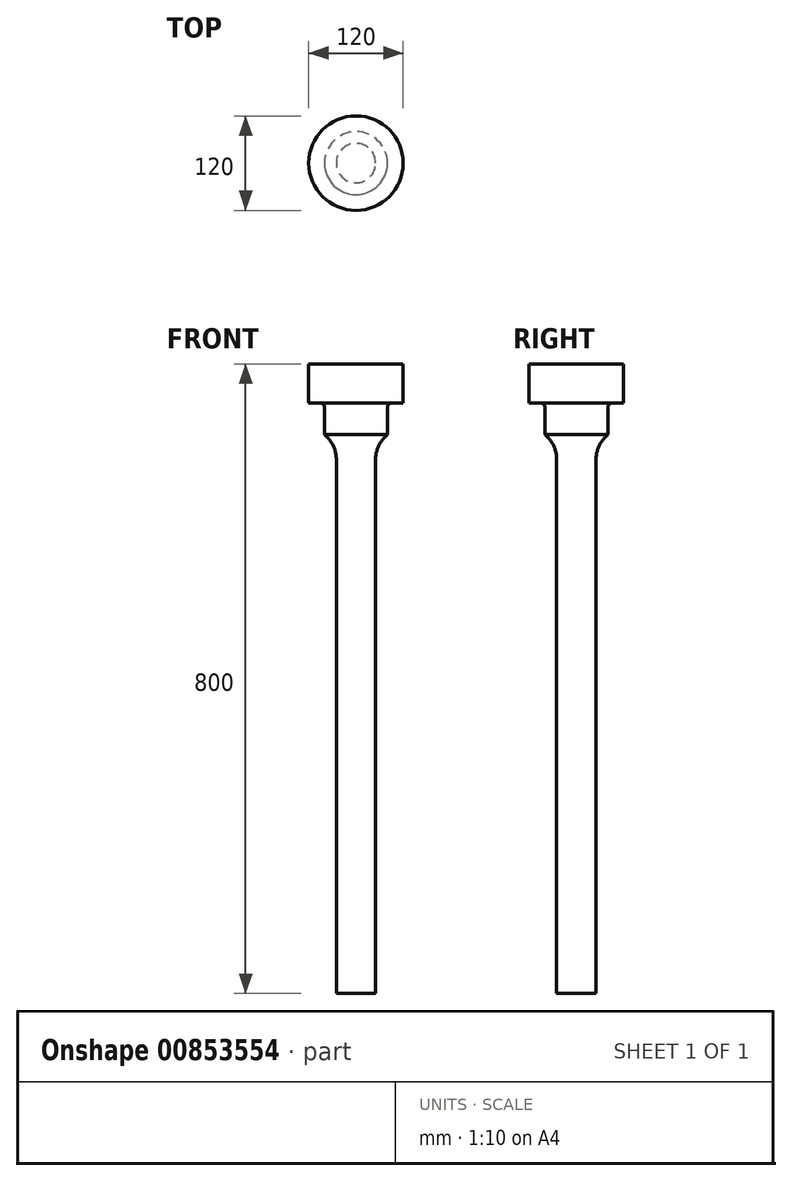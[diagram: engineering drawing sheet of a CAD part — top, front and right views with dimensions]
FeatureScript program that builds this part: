
annotation { "Feature Type Name" : "Feature", "Feature Type Description" : "" }
export const myFeature = defineFeature(function(context is Context, id is Id, definition is map)
    precondition{}
    {
        {
            var Q0;
            Q0=qCreatedBy(makeId("Front.planeOp"),FACE);
            var sketch = newSketch(context, id + "F0", { "sketchPlane" : qUnion([Q0])});
            skLineSegment(sketch, "E0", {"start": v(0, 0) * mm, "end": v(-60, 0) * mm});
            skLineSegment(sketch, "E1", {"start": v(-60, 0) * mm, "end": v(-60, -50) * mm});
            skLineSegment(sketch, "E2", {"start": v(-60, -50) * mm, "end": v(-40, -50) * mm});
            skLineSegment(sketch, "E3", {"start": v(-40, -50) * mm, "end": v(-40, -90) * mm});
            skLineSegment(sketch, "E4", {"start": v(-40, -90) * mm, "end": v(-25, -90) * mm});
            skLineSegment(sketch, "E5", {"start": v(-25, -90) * mm, "end": v(-25, -800) * mm});
            skLineSegment(sketch, "E6", {"start": v(-25, -800) * mm, "end": v(0, -800) * mm});
            skLineSegment(sketch, "E7", {"start": v(0, 0) * mm, "end": v(0, -800) * mm});
            skSolve(sketch);
        }
        {
            var Q0;
            Q0=makeQuery(id+"F0.imprint","IMPRINT",FACE,{"disambiguationData":[TD([[makeQuery(id+"F0.imprint","IMPRINT",EDGE,{"derivedFrom":sQuery(id+"F0.wireOp",EDGE,"E0")}),1.0]])]});
            var Q1;
            Q1=sQuery(id+"F0.wireOp",EDGE,"E7");
            revolve(context, id + "F1", {"surfaceOperationType" : NewSurfaceOperationType.NEW, "entities" : qUnion([Q0]), "axis" : qUnion([Q1]), "revolveType" : RevolveType.FULL});
        }
        {
            var Q0;
            Q0=makeQuery(id+"F1.opRevolve","SWEPT_EDGE",EDGE,{"disambiguationData":[OSD([sQuery(id+"F0.wireOp",EDGE,"E2"),sQuery(id+"F0.wireOp",EDGE,"E3")])]});
            fillet(context, id + "F2", {"entities" : qUnion([Q0]), "radius" : 5 * mm, "tangentPropagation" : true, "allowEdgeOverflow" : false});
        }
        {
            var Q0;
            Q0=makeQuery(id+"F1.opRevolve","SWEPT_EDGE",EDGE,{"disambiguationData":[OSD([sQuery(id+"F0.wireOp",EDGE,"E4"),sQuery(id+"F0.wireOp",EDGE,"E5")])]});
            fillet(context, id + "F3", {"entities" : qUnion([Q0]), "radius" : 40 * mm, "tangentPropagation" : true, "allowEdgeOverflow" : false});
        }
    });
